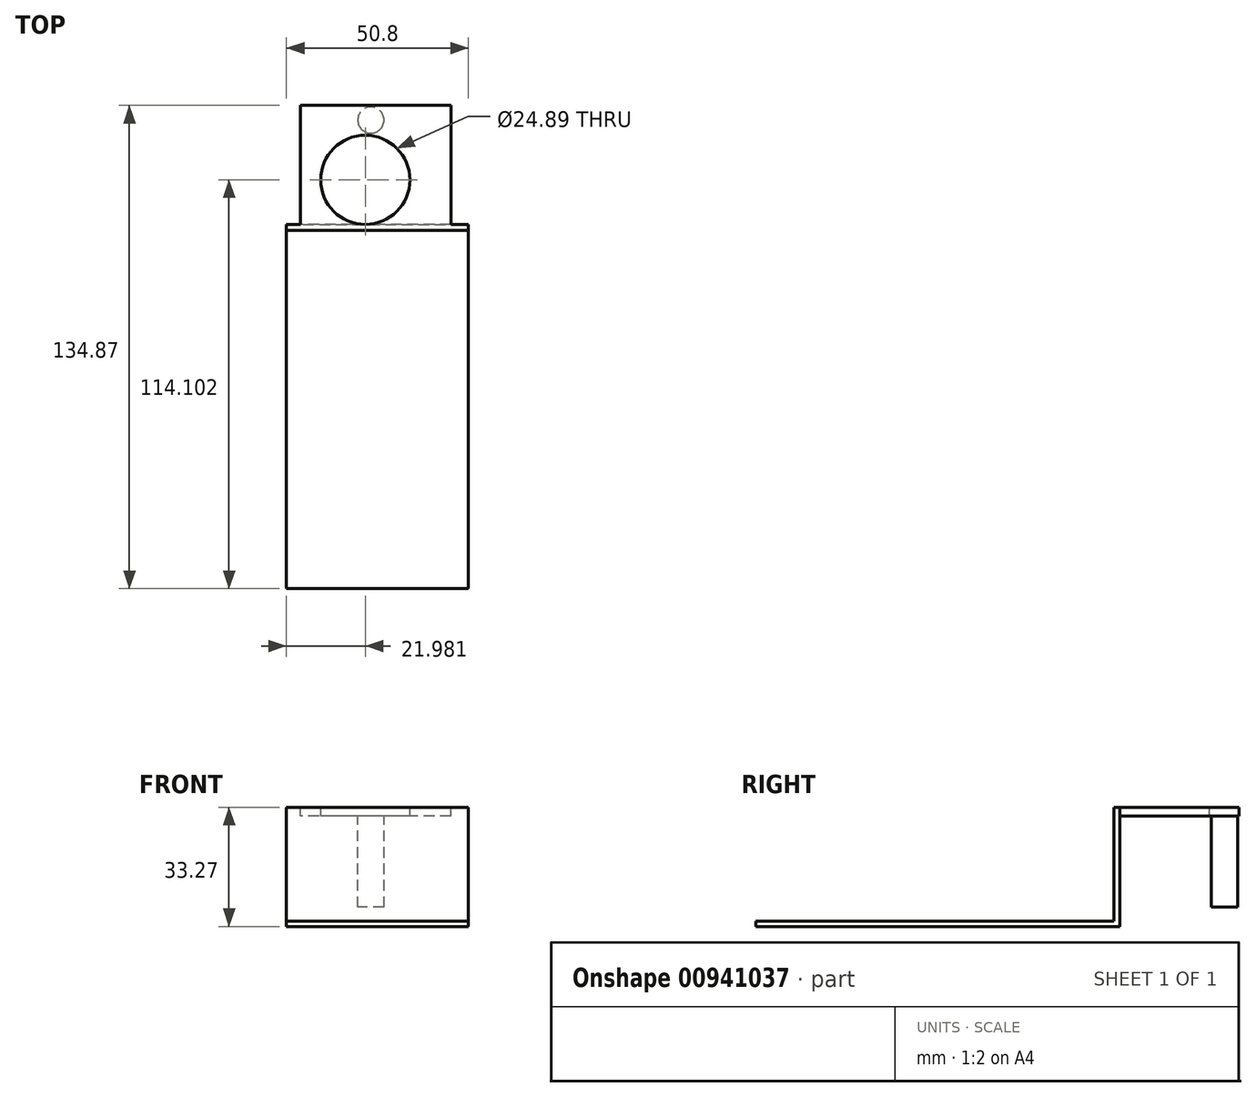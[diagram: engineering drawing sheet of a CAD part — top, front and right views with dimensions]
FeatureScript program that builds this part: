
annotation { "Feature Type Name" : "Feature", "Feature Type Description" : "" }
export const myFeature = defineFeature(function(context is Context, id is Id, definition is map)
    precondition{}
    {
        {
            var Q0;
            Q0=qCreatedBy(makeId("Top.planeOp"),FACE);
            var sketch = newSketch(context, id + "F0", { "sketchPlane" : qUnion([Q0])});
            skLineSegment(sketch, "E0.bottom", {"start": v(-39.1, 133.83) * mm, "end": v(11.7, 133.83) * mm});
            skLineSegment(sketch, "E0.top", {"start": v(-39.1, 32.23) * mm, "end": v(11.7, 32.23) * mm});
            skLineSegment(sketch, "E0.left", {"start": v(-39.1, 133.83) * mm, "end": v(-39.1, 32.23) * mm});
            skLineSegment(sketch, "E0.right", {"start": v(11.7, 133.83) * mm, "end": v(11.7, 32.23) * mm});
            skLineSegment(sketch, "E1", {"start": v(11.7, 132.16) * mm, "end": v(-39.1, 132.16) * mm});
            skSolve(sketch);
        }
        {
            var Q0;
            Q0 = qSketchRegion(id + "F0", true);
            extrude(context, id + "F1", {"entities" : qUnion([Q0]), "depth" : 1.52 * mm, "offsetDistance" : 25.4 * mm});
        }
        {
            var Q0;
            {var subQ0=sQuery(id+"F0.wireOp",EDGE,"E0.bottom");Q0=makeQuery(id+"F0.imprint","IMPRINT",FACE,{"disambiguationData":[TD([[makeQuery(id+"F0.imprint","IMPRINT",EDGE,{"derivedFrom":subQ0}),-1.0]])]});}
            extrude(context, id + "F2", {"entities" : qUnion([Q0]), "operationType" : NewBodyOperationType.ADD, "depth" : 33.27 * mm, "offsetDistance" : 25.4 * mm});
        }
        {
            var Q0;
            {var subQ0=sQuery(id+"F0.wireOp",EDGE,"E0.bottom");Q0=makeQuery(id+"F2.boolean.opBoolean","MERGE",FACE,{"derivedFrom":[makeQuery(id+"F1.opExtrude","SWEPT_FACE",FACE,{"disambiguationData":[OSD([subQ0])]}),makeQuery(id+"F2.opExtrude","SWEPT_FACE",FACE,{"disambiguationData":[OSD([subQ0])]})]});}
            var sketch = newSketch(context, id + "F3", { "sketchPlane" : qUnion([Q0])});
            skLineSegment(sketch, "E2", {"start": v(-6.79, 30.78) * mm, "end": v(35.22, 30.78) * mm});
            skLineSegment(sketch, "E3", {"start": v(-6.79, 30.78) * mm, "end": v(-6.79, 33.27) * mm});
            skLineSegment(sketch, "E4", {"start": v(35.22, 30.78) * mm, "end": v(35.22, 33.27) * mm});
            skSolve(sketch);
        }
        {
            var Q0;
            Q0 = qSketchRegion(id + "F3", true);
            var Q1;
            Q1=makeQuery(id+"F3.imprint","IMPRINT",FACE,{"disambiguationData":[TD([[makeQuery(id+"F3.imprint","IMPRINT",EDGE,{"derivedFrom":sQuery(id+"F3.wireOp",EDGE,"E2")}),1.0]])]});
            extrude(context, id + "F4", {"entities" : qUnion([Q0, Q1]), "operationType" : NewBodyOperationType.ADD, "depth" : 33.27 * mm, "offsetDistance" : 25.4 * mm});
        }
        {
            var Q0;
            {var subQ0=sQuery(id+"F0.wireOp",EDGE,"E0.bottom");Q0=makeQuery(id+"F4.boolean.opBoolean","MERGE",FACE,{"derivedFrom":[makeQuery(id+"F2.opExtrude","CAP_FACE",FACE,{"disambiguationData":[OSD([subQ0,sQuery(id+"F0.wireOp",EDGE,"E0.left"),sQuery(id+"F0.wireOp",EDGE,"E0.right"),sQuery(id+"F0.wireOp",EDGE,"E1")])],"isStart":false}),makeQuery(id+"F4.opExtrude","SWEPT_FACE",FACE,{"disambiguationData":[OSD([subQ0])]})]});}
            var sketch = newSketch(context, id + "F5", { "sketchPlane" : qUnion([Q0])});
            skCircle(sketch, "E5", {"center": v(-17.12, 146.33) * mm, "radius": 12.45 * mm});
            skSolve(sketch);
        }
        {
            var Q0;
            Q0 = qSketchRegion(id + "F5", true);
            extrude(context, id + "F6", {"entities" : qUnion([Q0]), "operationType" : NewBodyOperationType.REMOVE, "oppositeDirection" : true, "depth" : 25.4 * mm, "offsetDistance" : 25.4 * mm});
        }
        {
            var Q0;
            Q0=makeQuery(id+"F4.opExtrude","SWEPT_FACE",FACE,{"disambiguationData":[OSD([sQuery(id+"F3.wireOp",EDGE,"E2")])]});
            var sketch = newSketch(context, id + "F7", { "sketchPlane" : qUnion([Q0])});
            skCircle(sketch, "E6", {"center": v(-15.56, -163.02) * mm, "radius": 3.66 * mm});
            skSolve(sketch);
        }
        {
            var Q0;
            Q0 = qSketchRegion(id + "F7", true);
            extrude(context, id + "F8", {"entities" : qUnion([Q0]), "operationType" : NewBodyOperationType.ADD, "depth" : 25.4 * mm, "offsetDistance" : 25.4 * mm});
        }
    });
